# Revit family: WCBrushHolder-Vitra-BaseSeries-A44075
name_source: partatom
category: Plumbing Fixtures
revit_build: Autodesk Revit 2017 (Build: 20160225_1515(x64)
units: mm (PartAtom-declared; Revit-internal decimal feet)

## family parameters
Cut with Voids When Loaded = No
Host = Face
OmniClass Number = 23.45.00.00
OmniClass Title = Sanitary, Laundry, and Cleaning Equipment
Part Type = Normal
Room Calculation Point = No
Round Connector Dimension = Use Diameter
Shared = Yes

## types (2) — shared parameters
BIMobject category = Accessories
Brand = VitrA
CW Connection = No
Coating Material = <By Category>
Description = Base WC Brush Holder
Design country = Turkey
HW Connection = No
IFC Classification = Sanitary Terminal
Manufacturer = Vitra
Manufacturer name = Vitra
Masterformat 2014 Code = 10 28 13
Masterformat 2014 Description = Toilet Accessories
Mounting type = Wall Mounted
NBS Referans Code = 35-75-86
NBS Referans Description = Toilet Brush Holders
Nominal Depth (mm) = 130 mm  [stored 0.426509 ft]
Nominal Height (mm) = 360 mm  [stored 1.1811 ft]
Nominal Width (mm) = 115 mm
OmniClass Code = 23-31 25 00
OmniClass Description = Toilet and Bath Specialties
Product Type = WC Brush Holder
Product certification = https://www.vitraglobal.com
Product family = Base
Product group = Base WC Brush Holder
Product url = https://www.vitraglobal.com
Technical description = https://www.vitraglobal.com
UNSPSC Description = Plumbing Fixtures
URL = https://vitraglobal.com
Uniclass 1.4 Code = L7313
Uniclass 1.4 Description = Sanitary above ground pipes and fittings
Uniclass 2.0 Code = PR-35-75-86
Uniclass 2.0 Description = Toilet Brush Holders
Uniclass 2015 Code = PR_40_20_76_86
Uniclass 2015 Name = Toilet Brush Holders
Uniformat II Code = D2010
Uniformat II Description = Plumbing Fixtures
Vent Connection = No
Warranty Period (Year) = 5 Years
Waste Connection = No
Weight Net (kg) = 3
Youtube = https://www.youtube.com
zero-valued in all types: Default Elevation

## per-type parameters (varying)
| type | Article No. (default) | Color | Model | Primary Material | Product SKU |
| WCBrushHolder-Vitra-BaseSeries-A44075 | A44075 | Chrome | A44075 | Chrome | A44075 |
| WCBrushHolder-Vitra-BaseSeries-A4407536 | A4407536 | Matte Black | A4407536 | Matte Black (Metal) | A4407536 |

note: [stored X ft] marks values corroborated as IEEE doubles in the binary element streams (Revit-internal decimal feet)

## geometry (parser evidence)
native form markers: Sweep x3
no freeform markers — native parametric forms only
